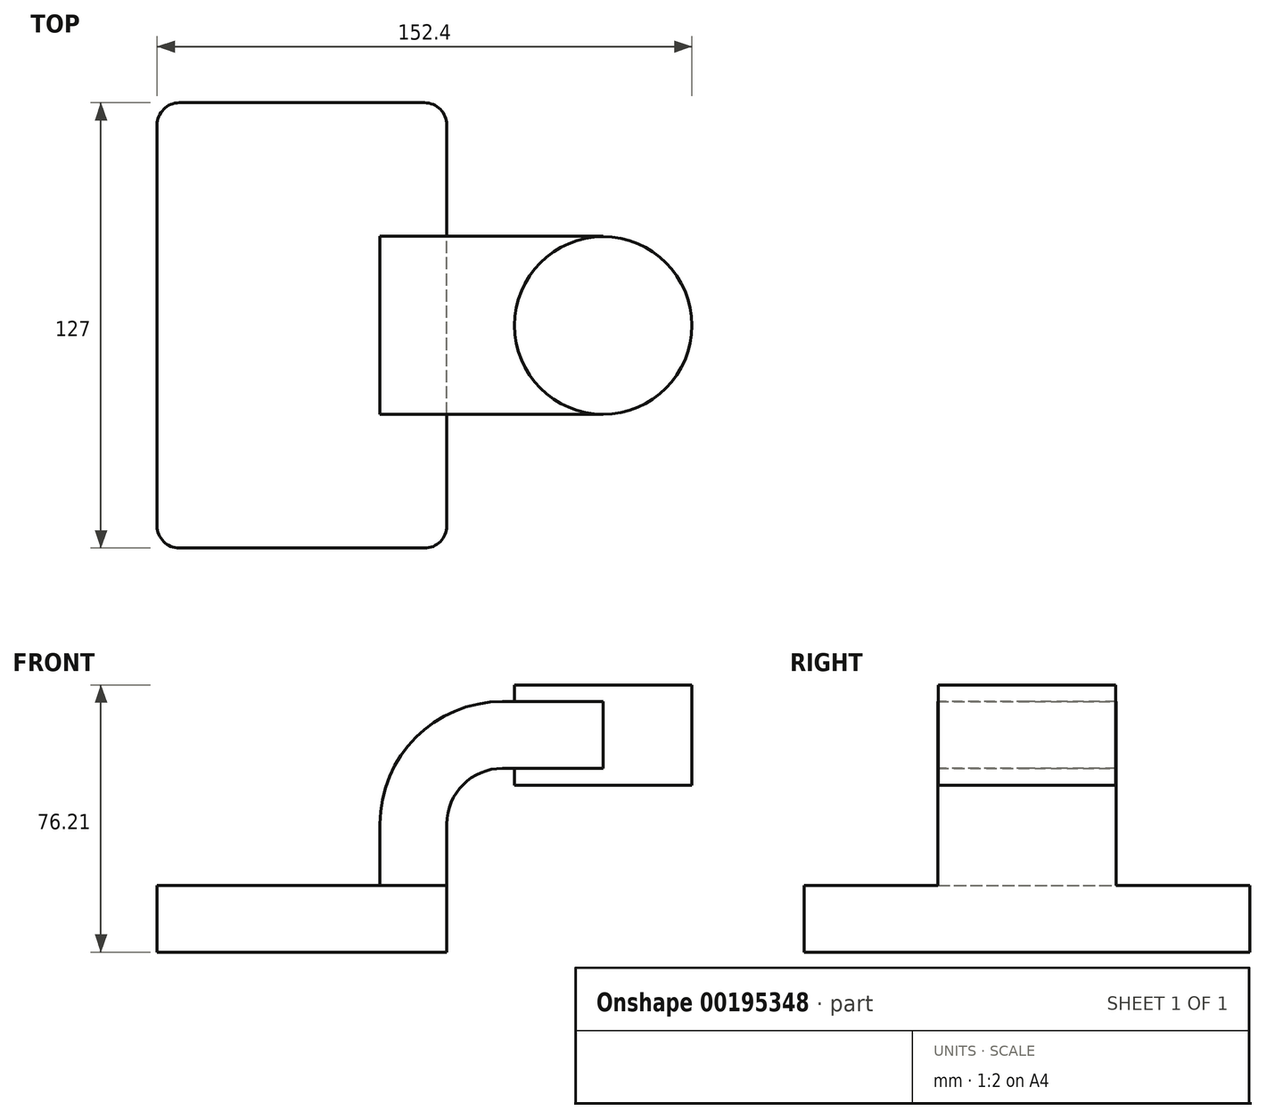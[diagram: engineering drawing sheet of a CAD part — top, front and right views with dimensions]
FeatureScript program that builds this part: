
annotation { "Feature Type Name" : "Feature", "Feature Type Description" : "" }
export const myFeature = defineFeature(function(context is Context, id is Id, definition is map)
    precondition{}
    {
        {
            var Q0;
            Q0=qCreatedBy(makeId("Front.planeOp"),FACE);
            var sketch = newSketch(context, id + "F0", { "sketchPlane" : qUnion([Q0])});
            skLineSegment(sketch, "E0.bottom", {"start": v(41.28, -9.52) * mm, "end": v(-41.28, -9.53) * mm});
            skLineSegment(sketch, "E0.top", {"start": v(41.28, 9.53) * mm, "end": v(-41.28, 9.53) * mm});
            skLineSegment(sketch, "E0.left", {"start": v(41.28, -9.52) * mm, "end": v(41.28, 9.53) * mm});
            skLineSegment(sketch, "E0.right", {"start": v(-41.28, -9.52) * mm, "end": v(-41.28, 9.53) * mm});
            skPoint(sketch, "E0.middle", {"position": v(0, 0) * mm});
            skLineSegment(sketch, "E1", {"start": v(41.28, 9.53) * mm, "end": v(41.28, 27) * mm});
            skLineSegment(sketch, "E2.bottom", {"start": v(111.12, 38.1) * mm, "end": v(60.32, 38.1) * mm});
            skLineSegment(sketch, "E2.top", {"start": v(111.12, 66.68) * mm, "end": v(60.32, 66.68) * mm});
            skLineSegment(sketch, "E2.left", {"start": v(111.12, 38.1) * mm, "end": v(111.12, 66.68) * mm});
            skLineSegment(sketch, "E2.right", {"start": v(60.32, 38.1) * mm, "end": v(60.32, 66.67) * mm});
            skPoint(sketch, "E2.middle", {"position": v(85.72, 52.39) * mm});
            skArc(sketch, "E3", {"start": v(41.27, 27) * mm, "mid": v(45.92, 38.23) * mm, "end": v(57.15, 42.88) * mm});
            skLineSegment(sketch, "E4", {"start": v(57.15, 42.88) * mm, "end": v(85.83, 42.88) * mm});
            skLineSegment(sketch, "E5.0", {"start": v(57.15, 61.93) * mm, "end": v(85.83, 61.93) * mm});
            skArc(sketch, "E5.1", {"start": v(22.23, 27) * mm, "mid": v(32.45, 51.7) * mm, "end": v(57.15, 61.93) * mm});
            skLineSegment(sketch, "E5.2", {"start": v(22.23, 9.53) * mm, "end": v(22.23, 27) * mm});
            skLineSegment(sketch, "E6", {"start": v(85.83, 38.1) * mm, "end": v(85.83, 66.68) * mm});
            skFitSpline(sketch, "E7", {"points": [v(-41.28, 9.53) * mm, v(57.15, 61.93) * mm], "startDerivative": vector(6.8, 105.24) * mm, "endDerivative": vector(114.77, -7.9) * mm});
            skSolve(sketch);
        }
        {
            var Q0;
            Q0=makeQuery(id+"F0.imprint","IMPRINT",FACE,{"disambiguationData":[TD([[makeQuery(id+"F0.imprint","IMPRINT",EDGE,{"derivedFrom":sQuery(id+"F0.wireOp",EDGE,"E0.bottom")}),-1.0]])]});
            extrude(context, id + "F1", {"entities" : qUnion([Q0]), "endBound" : BoundingType.SYMMETRIC, "depth" : 127 * mm});
        }
        {
            var Q0;
            {var subQ6=sQuery(id+"F0.wireOp",EDGE,"E1");Q0=makeQuery(id+"F0.imprint","IMPRINT",FACE,{"disambiguationData":[TD([[makeQuery(id+"F0.imprint","IMPRINT",EDGE,{"derivedFrom":subQ6}),1.0]])]});}
            var Q1;
            {var subQ0=sQuery(id+"F0.wireOp",EDGE,"E4");var subQ1=sQuery(id+"F0.wireOp",EDGE,"E2.right");var subQ2=makeQuery(id+"F0.imprint","INTERSECT",VERTEX,{"derivedFrom":[subQ1,subQ0]});Q1=makeQuery(id+"F0.imprint","IMPRINT",FACE,{"disambiguationData":[TD([[makeQuery(id+"F0.imprint","IMPRINT",EDGE,{"disambiguationData":[TD([[subQ2,-1.0]])],"derivedFrom":subQ1}),-1.0]])]});}
            extrude(context, id + "F2", {"entities" : qUnion([Q0, Q1]), "operationType" : NewBodyOperationType.ADD, "endBound" : BoundingType.SYMMETRIC, "depth" : 50.8 * mm});
        }
        {
            var Q0;
            Q0=makeQuery(id+"F0.imprint","IMPRINT",FACE,{"disambiguationData":[TD([[makeQuery(id+"F0.imprint","IMPRINT",EDGE,{"derivedFrom":sQuery(id+"F0.wireOp",EDGE,"E5.1")}),1.0]])]});
            extrude(context, id + "F3", {"entities" : qUnion([Q0]), "operationType" : NewBodyOperationType.ADD, "endBound" : BoundingType.SYMMETRIC, "depth" : 15.88 * mm});
        }
        {
            var Q0;
            {var subQ0=sQuery(id+"F0.wireOp",EDGE,"E2.left");Q0=makeQuery(id+"F0.imprint","IMPRINT",FACE,{"disambiguationData":[TD([[makeQuery(id+"F0.imprint","IMPRINT",EDGE,{"derivedFrom":subQ0}),1.0]])]});}
            var Q1;
            Q1=sQuery(id+"F0.wireOp",EDGE,"E6");
            revolve(context, id + "F4", {"operationType" : NewBodyOperationType.ADD, "entities" : qUnion([Q0]), "axis" : qUnion([Q1]), "revolveType" : RevolveType.FULL});
        }
        {
            var Q0;
            Q0=makeQuery(id+"F1.opExtrude","CAP_EDGE",EDGE,{"disambiguationData":[OSD([sQuery(id+"F0.wireOp",EDGE,"E0.right")])],"isStart":false});
            var Q1;
            Q1=makeQuery(id+"F1.opExtrude","CAP_EDGE",EDGE,{"disambiguationData":[OSD([sQuery(id+"F0.wireOp",EDGE,"E0.left")])],"isStart":false});
            var Q2;
            Q2=makeQuery(id+"F1.opExtrude","CAP_EDGE",EDGE,{"disambiguationData":[OSD([sQuery(id+"F0.wireOp",EDGE,"E0.left")])],"isStart":true});
            var Q3;
            Q3=makeQuery(id+"F1.opExtrude","CAP_EDGE",EDGE,{"disambiguationData":[OSD([sQuery(id+"F0.wireOp",EDGE,"E0.right")])],"isStart":true});
            fillet(context, id + "F5", {"entities" : qUnion([Q0, Q1, Q2, Q3]), "radius" : 6.35 * mm, "tangentPropagation" : true, "allowEdgeOverflow" : false});
        }
    });
